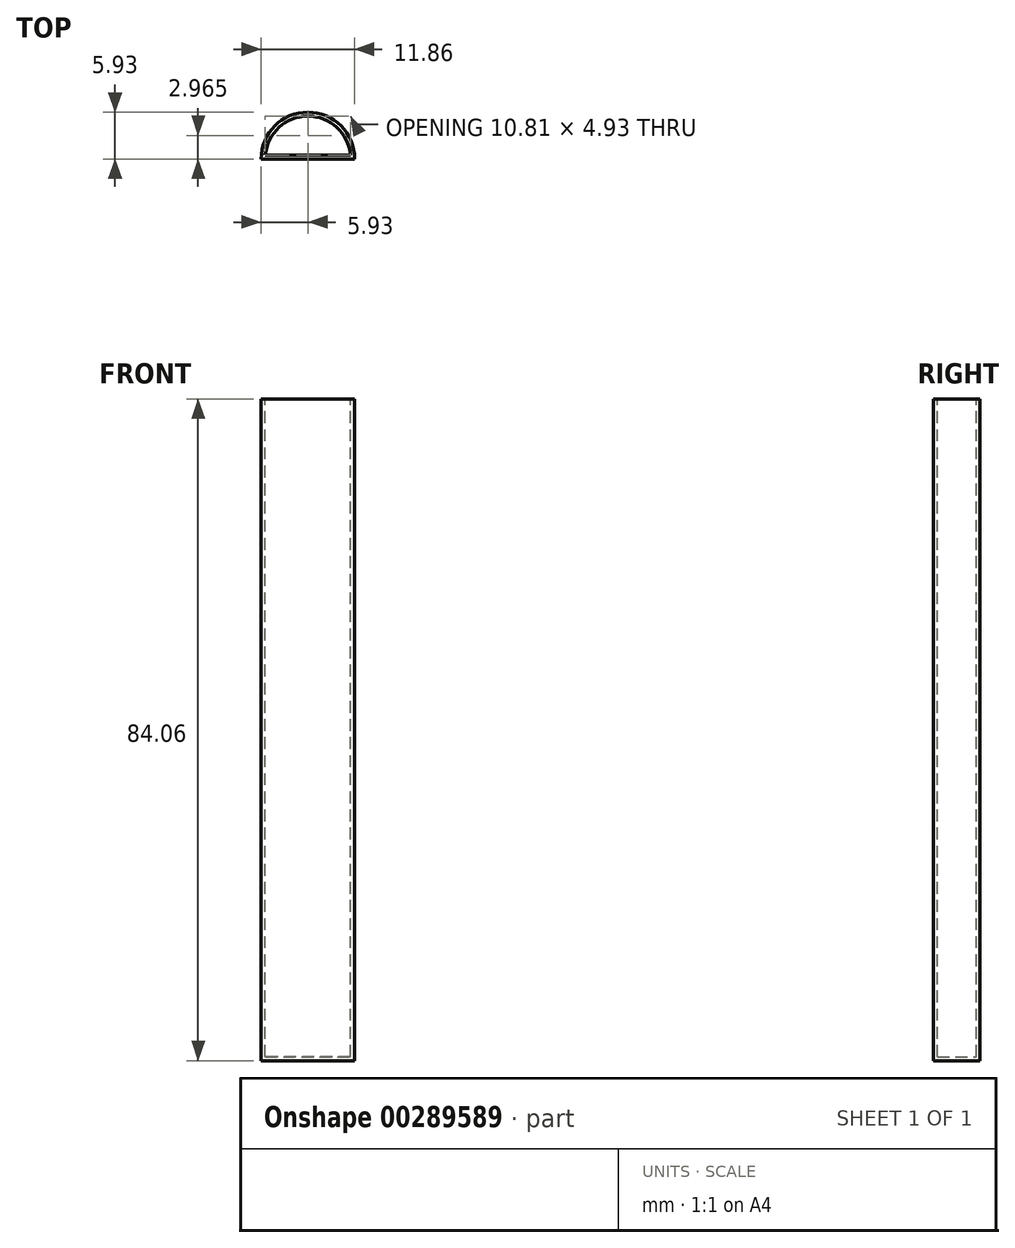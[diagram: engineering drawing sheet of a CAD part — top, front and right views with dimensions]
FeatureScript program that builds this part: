
annotation { "Feature Type Name" : "Feature", "Feature Type Description" : "" }
export const myFeature = defineFeature(function(context is Context, id is Id, definition is map)
    precondition{}
    {
        {
            var Q0;
            Q0=qCreatedBy(makeId("Right.planeOp"),FACE);
            var sketch = newSketch(context, id + "F0", { "sketchPlane" : qUnion([Q0])});
            skLineSegment(sketch, "E0.bottom", {"start": v(5.93, 42.03) * mm, "end": v(-5.93, 42.03) * mm});
            skLineSegment(sketch, "E0.top", {"start": v(5.93, -42.03) * mm, "end": v(-5.93, -42.03) * mm});
            skLineSegment(sketch, "E0.left", {"start": v(5.93, 42.03) * mm, "end": v(5.93, -42.03) * mm});
            skLineSegment(sketch, "E0.right", {"start": v(-5.93, 42.03) * mm, "end": v(-5.93, -42.03) * mm});
            skPoint(sketch, "E0.middle", {"position": v(0, 0) * mm});
            skLineSegment(sketch, "E1", {"start": v(0, 42.03) * mm, "end": v(0, -42.03) * mm});
            skSolve(sketch);
        }
        {
            var Q0;
            {var subQ0=sQuery(id+"F0.wireOp",EDGE,"E0.left");Q0=makeQuery(id+"F0.imprint","IMPRINT",FACE,{"disambiguationData":[TD([[makeQuery(id+"F0.imprint","IMPRINT",EDGE,{"derivedFrom":subQ0}),-1.0]])]});}
            var Q1;
            Q1=sQuery(id+"F0.wireOp",EDGE,"E1");
            revolve(context, id + "F1", {"entities" : qUnion([Q0]), "axis" : qUnion([Q1]), "revolveType" : RevolveType.SYMMETRIC, "angle" : 180 * degree});
        }
        {
            var Q0;
            Q0=makeQuery(id+"F1.opRevolve","SWEPT_FACE",FACE,{"disambiguationData":[OSD([sQuery(id+"F0.wireOp",EDGE,"E0.bottom")])]});
            shell(context, id + "F2", {"entities" : qUnion([Q0]), "thickness" : .5 * mm});
        }
    });
